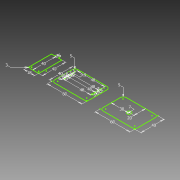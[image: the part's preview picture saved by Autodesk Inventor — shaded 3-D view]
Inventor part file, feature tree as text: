
AUTODESK INVENTOR PART (.ipt)
format: ipt  version: 2012 (Build 160160000, 160)  size: 95,232 bytes
history: native  units: mm
features: sketch x1
ambient origin geometry x8: Origin, YZ Plane, XZ Plane, XY Plane, X Axis, Y Axis, Z Axis, Center Point
feature tree (1):
  sketch  "Sketch1"  dims[d0=18.0mm d1=40.0mm d3=3.0mm d4=6.0mm d5=60.0mm d7=3.0mm d8=3.0mm d9=3.0mm d10=3.0mm d11=5.0mm d12=3.0mm d13=5.0mm d14=5.0mm d15=48.0mm d16=48.0mm d17=48.0mm d18=48.0mm d20=6.0mm d21=6.0mm d22=6.0mm d23=6.0mm d25=9.5mm d26=5.0mm d27=5.0mm d28=5.0mm d29=40.0mm d30=40.0mm d31=3.0mm d32=5.0mm d33=60.0mm d34=40.0mm d35=5.0mm d36=7.0mm d37=30.0mm d38=20.0mm]
